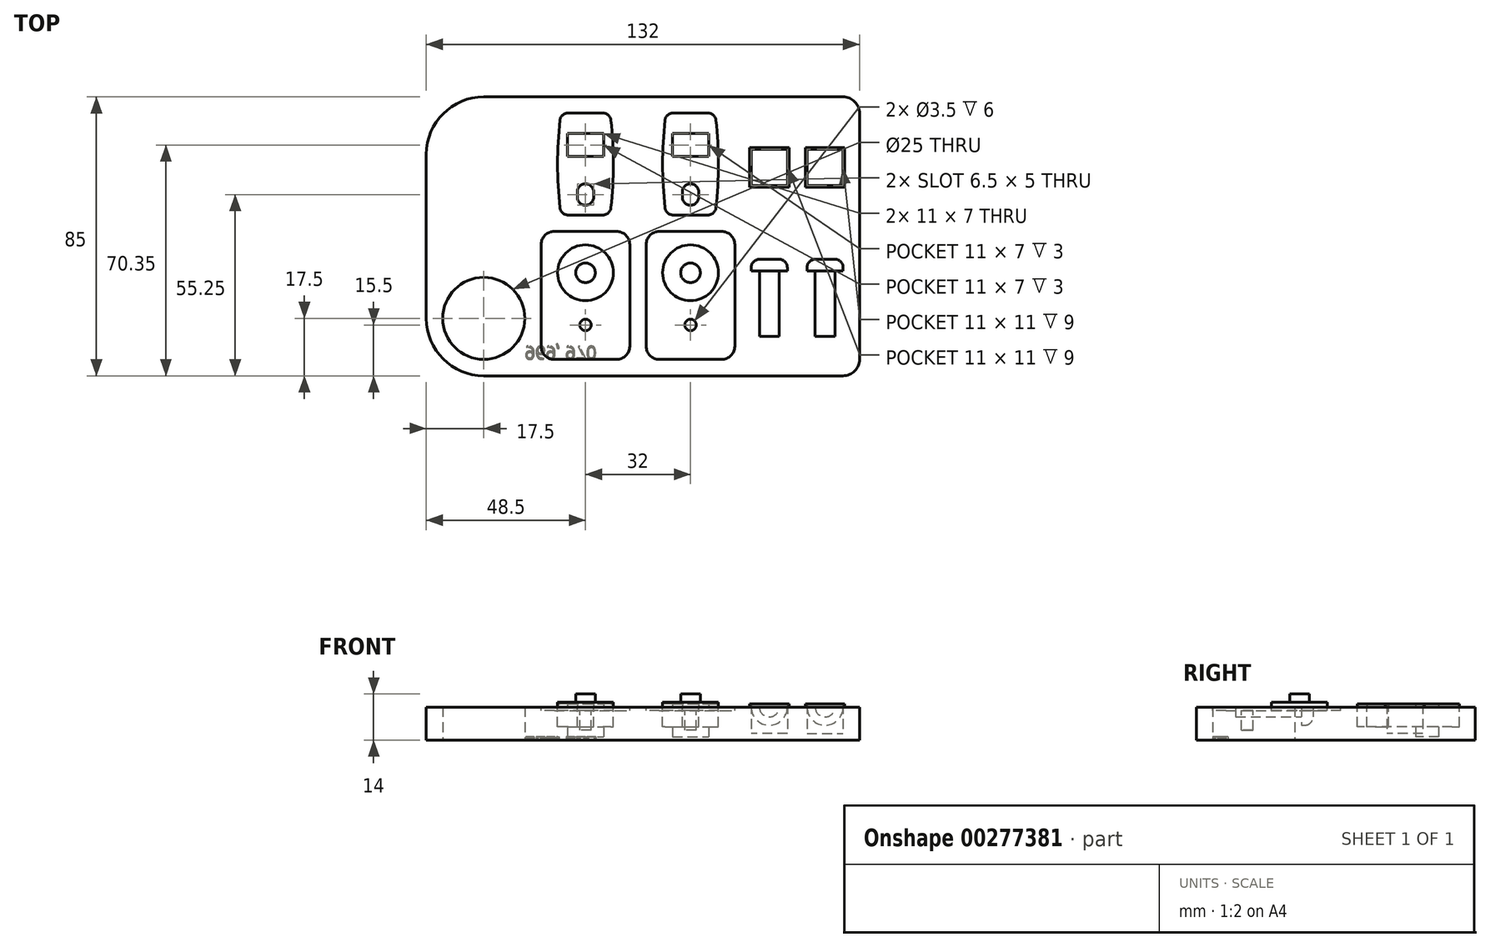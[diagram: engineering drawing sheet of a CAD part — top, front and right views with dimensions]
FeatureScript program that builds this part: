
annotation { "Feature Type Name" : "Feature", "Feature Type Description" : "" }
export const myFeature = defineFeature(function(context is Context, id is Id, definition is map)
    precondition{}
    {
        {
            var Q0;
            Q0=qCreatedBy(makeId("Top.planeOp"),FACE);
            var sketch = newSketch(context, id + "F0", { "sketchPlane" : qUnion([Q0])});
            skLineSegment(sketch, "E0.bottom", {"start": v(17.5, 0) * mm, "end": v(127, 0) * mm});
            skLineSegment(sketch, "E0.top", {"start": v(17.5, 85) * mm, "end": v(127, 85) * mm});
            skLineSegment(sketch, "E0.left", {"start": v(0, 17.5) * mm, "end": v(0, 67.5) * mm});
            skLineSegment(sketch, "E0.right", {"start": v(132, 5) * mm, "end": v(132, 80) * mm});
            skLineSegment(sketch, "E1.bottom", {"start": v(0, 0) * mm, "end": v(17.5, 0) * mm, "construction": true});
            skLineSegment(sketch, "E1.top", {"start": v(0, 17.5) * mm, "end": v(17.5, 17.5) * mm, "construction": true});
            skLineSegment(sketch, "E1.left", {"start": v(0, 0) * mm, "end": v(0, 17.5) * mm, "construction": true});
            skLineSegment(sketch, "E1.right", {"start": v(17.5, 0) * mm, "end": v(17.5, 17.5) * mm, "construction": true});
            skCircle(sketch, "E2", {"center": v(17.5, 17.5) * mm, "radius": 12.5 * mm});
            skPoint(sketch, "E3.visualSharp", {"position": v(0, 0) * mm});
            skArc(sketch, "E3.filletArc", {"start": v(0, 17.5) * mm, "mid": v(5.13, 5.13) * mm, "end": v(17.5, 0) * mm});
            skPoint(sketch, "E4.visualSharp", {"position": v(0, 85) * mm});
            skArc(sketch, "E4.filletArc", {"start": v(17.5, 85) * mm, "mid": v(5.13, 79.87) * mm, "end": v(0, 67.5) * mm});
            skPoint(sketch, "E5.visualSharp", {"position": v(132, 85) * mm});
            skArc(sketch, "E5.filletArc", {"start": v(132, 80) * mm, "mid": v(130.54, 83.54) * mm, "end": v(127, 85) * mm});
            skPoint(sketch, "E6.visualSharp", {"position": v(132, 0) * mm});
            skArc(sketch, "E6.filletArc", {"start": v(127, 0) * mm, "mid": v(130.54, 1.46) * mm, "end": v(132, 5) * mm});
            skSolve(sketch);
        }
        {
            var Q0;
            Q0=makeQuery(id+"F0.imprint","IMPRINT",FACE,{"disambiguationData":[TD([[makeQuery(id+"F0.imprint","IMPRINT",EDGE,{"derivedFrom":sQuery(id+"F0.wireOp",EDGE,"E0.bottom")}),1.0]])]});
            extrude(context, id + "F1", {"entities" : qUnion([Q0]), "depth" : 10 * mm});
        }
        {
            var Q0;
            Q0=makeQuery(id+"F1.opExtrude","CAP_FACE",FACE,{"disambiguationData":[OSD([sQuery(id+"F0.wireOp",EDGE,"E0.bottom"),sQuery(id+"F0.wireOp",EDGE,"E0.top"),sQuery(id+"F0.wireOp",EDGE,"E0.left"),sQuery(id+"F0.wireOp",EDGE,"E0.right"),sQuery(id+"F0.wireOp",EDGE,"E2"),sQuery(id+"F0.wireOp",EDGE,"E3.filletArc"),sQuery(id+"F0.wireOp",EDGE,"E4.filletArc"),sQuery(id+"F0.wireOp",EDGE,"E5.filletArc"),sQuery(id+"F0.wireOp",EDGE,"E6.filletArc")])],"isStart":false});
            var sketch = newSketch(context, id + "F2", { "sketchPlane" : qUnion([Q0])});
            skLineSegment(sketch, "E7.bottom", {"start": v(0, 0) * mm, "end": v(35, 0) * mm, "construction": true});
            skLineSegment(sketch, "E7.top", {"start": v(0, 5) * mm, "end": v(35, 5) * mm, "construction": true});
            skLineSegment(sketch, "E7.left", {"start": v(0, 0) * mm, "end": v(0, 5) * mm, "construction": true});
            skLineSegment(sketch, "E7.right", {"start": v(35, 0) * mm, "end": v(35, 5) * mm, "construction": true});
            skLineSegment(sketch, "E8.bottom", {"start": v(39, 5) * mm, "end": v(58, 5) * mm});
            skLineSegment(sketch, "E8.top", {"start": v(39, 44) * mm, "end": v(58, 44) * mm});
            skLineSegment(sketch, "E8.left", {"start": v(35, 9) * mm, "end": v(35, 40) * mm});
            skLineSegment(sketch, "E8.right", {"start": v(62, 9) * mm, "end": v(62, 40) * mm});
            skLineSegment(sketch, "E9", {"start": v(62, 5) * mm, "end": v(67, 5) * mm, "construction": true});
            skLineSegment(sketch, "E10.bottom", {"start": v(71, 5) * mm, "end": v(90, 5) * mm});
            skLineSegment(sketch, "E10.top", {"start": v(71, 44) * mm, "end": v(90, 44) * mm});
            skLineSegment(sketch, "E10.left", {"start": v(67, 9) * mm, "end": v(67, 40) * mm});
            skLineSegment(sketch, "E10.right", {"start": v(94, 9) * mm, "end": v(94, 40) * mm});
            skPoint(sketch, "E11.visualSharp", {"position": v(35, 44) * mm});
            skArc(sketch, "E11.filletArc", {"start": v(39, 44) * mm, "mid": v(36.17, 42.83) * mm, "end": v(35, 40) * mm});
            skPoint(sketch, "E12.visualSharp", {"position": v(62, 44) * mm});
            skArc(sketch, "E12.filletArc", {"start": v(62, 40) * mm, "mid": v(60.83, 42.83) * mm, "end": v(58, 44) * mm});
            skPoint(sketch, "E13.visualSharp", {"position": v(35, 5) * mm});
            skArc(sketch, "E13.filletArc", {"start": v(35, 9) * mm, "mid": v(36.17, 6.17) * mm, "end": v(39, 5) * mm});
            skPoint(sketch, "E14.visualSharp", {"position": v(62, 5) * mm});
            skArc(sketch, "E14.filletArc", {"start": v(58, 5) * mm, "mid": v(60.83, 6.17) * mm, "end": v(62, 9) * mm});
            skPoint(sketch, "E15.visualSharp", {"position": v(67, 5) * mm});
            skArc(sketch, "E15.filletArc", {"start": v(67, 9) * mm, "mid": v(68.17, 6.17) * mm, "end": v(71, 5) * mm});
            skPoint(sketch, "E16.visualSharp", {"position": v(67, 44) * mm});
            skArc(sketch, "E16.filletArc", {"start": v(71, 44) * mm, "mid": v(68.17, 42.83) * mm, "end": v(67, 40) * mm});
            skPoint(sketch, "E17.visualSharp", {"position": v(94, 44) * mm});
            skArc(sketch, "E17.filletArc", {"start": v(94, 40) * mm, "mid": v(92.83, 42.83) * mm, "end": v(90, 44) * mm});
            skPoint(sketch, "E18.visualSharp", {"position": v(94, 5) * mm});
            skArc(sketch, "E18.filletArc", {"start": v(90, 5) * mm, "mid": v(92.83, 6.17) * mm, "end": v(94, 9) * mm});
            skPoint(sketch, "E19.oppositeSnap0", {"position": v(48.5, 5) * mm});
            skLineSegment(sketch, "E19.bottom", {"start": v(35, 5) * mm, "end": v(48.5, 5) * mm, "construction": true});
            skLineSegment(sketch, "E19.top", {"start": v(35, 15.5) * mm, "end": v(48.5, 15.5) * mm, "construction": true});
            skLineSegment(sketch, "E19.left", {"start": v(35, 5) * mm, "end": v(35, 15.5) * mm, "construction": true});
            skLineSegment(sketch, "E19.right", {"start": v(48.5, 5) * mm, "end": v(48.5, 15.5) * mm, "construction": true});
            skLineSegment(sketch, "E20", {"start": v(48.5, 44) * mm, "end": v(48.5, 31.4) * mm, "construction": true});
            skLineSegment(sketch, "E21", {"start": v(80.5, 44) * mm, "end": v(80.5, 31.4) * mm, "construction": true});
            skLineSegment(sketch, "E22", {"start": v(80.5, 5) * mm, "end": v(80.5, 15.5) * mm, "construction": true});
            skCircle(sketch, "E23", {"center": v(48.5, 31.4) * mm, "radius": 8.5 * mm});
            skCircle(sketch, "E24", {"center": v(48.5, 31.4) * mm, "radius": 3 * mm});
            skCircle(sketch, "E25", {"center": v(48.5, 15.5) * mm, "radius": 1.75 * mm});
            skCircle(sketch, "E26", {"center": v(80.5, 15.5) * mm, "radius": 1.75 * mm});
            skCircle(sketch, "E27", {"center": v(80.5, 31.4) * mm, "radius": 3 * mm});
            skCircle(sketch, "E28", {"center": v(80.5, 31.4) * mm, "radius": 8.5 * mm});
            skLineSegment(sketch, "E29.bottom", {"start": v(94, 5) * mm, "end": v(104.5, 5) * mm, "construction": true});
            skLineSegment(sketch, "E29.top", {"start": v(94, 12) * mm, "end": v(104.5, 12) * mm, "construction": true});
            skLineSegment(sketch, "E29.left", {"start": v(94, 5) * mm, "end": v(94, 12) * mm, "construction": true});
            skLineSegment(sketch, "E29.right", {"start": v(104.5, 5) * mm, "end": v(104.5, 12) * mm, "construction": true});
            skLineSegment(sketch, "E30", {"start": v(104.5, 12) * mm, "end": v(121.5, 12) * mm, "construction": true});
            skLineSegment(sketch, "E31.bottom", {"start": v(104.5, 12) * mm, "end": v(107.5, 12) * mm});
            skLineSegment(sketch, "E31.left", {"start": v(104.5, 12) * mm, "end": v(104.5, 32) * mm});
            skLineSegment(sketch, "E31.right", {"start": v(107.5, 12) * mm, "end": v(107.5, 32) * mm});
            skLineSegment(sketch, "E32.bottom", {"start": v(107.5, 32) * mm, "end": v(110, 32) * mm});
            skLineSegment(sketch, "E32.top", {"start": v(104.5, 35.5) * mm, "end": v(107.5, 35.5) * mm});
            skLineSegment(sketch, "E32.left", {"start": v(104.5, 32) * mm, "end": v(104.5, 35.5) * mm});
            skLineSegment(sketch, "E32.right", {"start": v(110, 32) * mm, "end": v(110, 33) * mm});
            skPoint(sketch, "E33.visualSharp", {"position": v(110, 35.5) * mm});
            skArc(sketch, "E33.filletArc", {"start": v(110, 33) * mm, "mid": v(109.27, 34.77) * mm, "end": v(107.5, 35.5) * mm});
            skLineSegment(sketch, "E34.bottom", {"start": v(121.5, 12) * mm, "end": v(124.5, 12) * mm});
            skLineSegment(sketch, "E34.left", {"start": v(121.5, 12) * mm, "end": v(121.5, 32) * mm});
            skLineSegment(sketch, "E34.right", {"start": v(124.5, 12) * mm, "end": v(124.5, 32) * mm});
            skLineSegment(sketch, "E35.bottom", {"start": v(124.5, 32) * mm, "end": v(127, 32) * mm});
            skLineSegment(sketch, "E35.top", {"start": v(121.5, 35.5) * mm, "end": v(124.5, 35.5) * mm});
            skLineSegment(sketch, "E35.left", {"start": v(121.5, 32) * mm, "end": v(121.5, 35.5) * mm});
            skLineSegment(sketch, "E35.right", {"start": v(127, 32) * mm, "end": v(127, 33) * mm});
            skPoint(sketch, "E36.visualSharp", {"position": v(127, 35.5) * mm});
            skArc(sketch, "E36.filletArc", {"start": v(127, 33) * mm, "mid": v(126.27, 34.77) * mm, "end": v(124.5, 35.5) * mm});
            skLineSegment(sketch, "E37.bottom", {"start": v(35, 44) * mm, "end": v(41, 44) * mm, "construction": true});
            skLineSegment(sketch, "E37.top", {"start": v(35, 49) * mm, "end": v(41, 49) * mm, "construction": true});
            skLineSegment(sketch, "E37.left", {"start": v(35, 44) * mm, "end": v(35, 49) * mm, "construction": true});
            skLineSegment(sketch, "E37.right", {"start": v(41, 44) * mm, "end": v(41, 49) * mm, "construction": true});
            skLineSegment(sketch, "E38.bottom", {"start": v(43.22, 49) * mm, "end": v(53.78, 49) * mm});
            skLineSegment(sketch, "E38.top", {"start": v(43.22, 80.1) * mm, "end": v(53.78, 80.1) * mm});
            skLineSegment(sketch, "E38.left", {"start": v(41, 49) * mm, "end": v(41, 80.1) * mm, "construction": true});
            skLineSegment(sketch, "E38.right", {"start": v(56, 49) * mm, "end": v(56, 80.1) * mm, "construction": true});
            skLineSegment(sketch, "E39.bottom", {"start": v(67, 44) * mm, "end": v(73, 44) * mm, "construction": true});
            skLineSegment(sketch, "E39.top", {"start": v(67, 49) * mm, "end": v(73, 49) * mm, "construction": true});
            skLineSegment(sketch, "E39.left", {"start": v(67, 44) * mm, "end": v(67, 49) * mm, "construction": true});
            skLineSegment(sketch, "E39.right", {"start": v(73, 44) * mm, "end": v(73, 49) * mm, "construction": true});
            skLineSegment(sketch, "E40.bottom", {"start": v(75.22, 49) * mm, "end": v(85.78, 49) * mm});
            skLineSegment(sketch, "E40.top", {"start": v(75.22, 80.1) * mm, "end": v(85.78, 80.1) * mm});
            skLineSegment(sketch, "E40.left", {"start": v(73, 49) * mm, "end": v(73, 80.1) * mm, "construction": true});
            skLineSegment(sketch, "E40.right", {"start": v(88, 49) * mm, "end": v(88, 80.1) * mm, "construction": true});
            skLineSegment(sketch, "E41", {"start": v(41, 64.55) * mm, "end": v(40, 64.55) * mm});
            skLineSegment(sketch, "E42", {"start": v(56, 64.55) * mm, "end": v(57, 64.55) * mm});
            skLineSegment(sketch, "E43", {"start": v(73, 64.55) * mm, "end": v(72, 64.55) * mm});
            skLineSegment(sketch, "E44", {"start": v(88, 64.55) * mm, "end": v(89, 64.55) * mm});
            skArc(sketch, "E45", {"start": v(40.73, 77.87) * mm, "mid": v(40, 64.55) * mm, "end": v(40.73, 51.23) * mm});
            skArc(sketch, "E46", {"start": v(56.27, 51.23) * mm, "mid": v(57, 64.55) * mm, "end": v(56.27, 77.87) * mm});
            skArc(sketch, "E47", {"start": v(72.73, 77.87) * mm, "mid": v(72, 64.55) * mm, "end": v(72.73, 51.23) * mm});
            skArc(sketch, "E48", {"start": v(88.27, 51.23) * mm, "mid": v(89, 64.55) * mm, "end": v(88.27, 77.87) * mm});
            skPoint(sketch, "E49.visualSharp", {"position": v(56, 80.1) * mm});
            skArc(sketch, "E49.filletArc", {"start": v(56.27, 77.87) * mm, "mid": v(55.45, 79.46) * mm, "end": v(53.78, 80.1) * mm});
            skPoint(sketch, "E50.visualSharp", {"position": v(41, 80.1) * mm});
            skArc(sketch, "E50.filletArc", {"start": v(43.22, 80.1) * mm, "mid": v(41.55, 79.46) * mm, "end": v(40.73, 77.87) * mm});
            skPoint(sketch, "E51.visualSharp", {"position": v(41, 49) * mm});
            skArc(sketch, "E51.filletArc", {"start": v(40.73, 51.23) * mm, "mid": v(41.55, 49.64) * mm, "end": v(43.22, 49) * mm});
            skPoint(sketch, "E52.visualSharp", {"position": v(56, 49) * mm});
            skArc(sketch, "E52.filletArc", {"start": v(53.78, 49) * mm, "mid": v(55.45, 49.64) * mm, "end": v(56.27, 51.23) * mm});
            skPoint(sketch, "E53.visualSharp", {"position": v(73, 49) * mm});
            skArc(sketch, "E53.filletArc", {"start": v(72.73, 51.23) * mm, "mid": v(73.55, 49.64) * mm, "end": v(75.22, 49) * mm});
            skPoint(sketch, "E54.visualSharp", {"position": v(88, 49) * mm});
            skArc(sketch, "E54.filletArc", {"start": v(85.78, 49) * mm, "mid": v(87.45, 49.64) * mm, "end": v(88.27, 51.23) * mm});
            skPoint(sketch, "E55.visualSharp", {"position": v(88, 80.1) * mm});
            skArc(sketch, "E55.filletArc", {"start": v(88.27, 77.87) * mm, "mid": v(87.45, 79.46) * mm, "end": v(85.78, 80.1) * mm});
            skPoint(sketch, "E56.visualSharp", {"position": v(73, 80.1) * mm});
            skArc(sketch, "E56.filletArc", {"start": v(75.22, 80.1) * mm, "mid": v(73.55, 79.46) * mm, "end": v(72.73, 77.87) * mm});
            skLineSegment(sketch, "E57.bottom", {"start": v(41, 80.1) * mm, "end": v(43, 80.1) * mm, "construction": true});
            skLineSegment(sketch, "E57.top", {"start": v(41, 73.85) * mm, "end": v(43, 73.85) * mm, "construction": true});
            skLineSegment(sketch, "E57.left", {"start": v(41, 80.1) * mm, "end": v(41, 73.85) * mm, "construction": true});
            skLineSegment(sketch, "E57.right", {"start": v(43, 80.1) * mm, "end": v(43, 73.85) * mm, "construction": true});
            skLineSegment(sketch, "E58.bottom", {"start": v(73, 80.1) * mm, "end": v(75, 80.1) * mm, "construction": true});
            skLineSegment(sketch, "E58.top", {"start": v(73, 73.85) * mm, "end": v(75, 73.85) * mm, "construction": true});
            skLineSegment(sketch, "E58.left", {"start": v(73, 80.1) * mm, "end": v(73, 73.85) * mm, "construction": true});
            skLineSegment(sketch, "E58.right", {"start": v(75, 80.1) * mm, "end": v(75, 73.85) * mm, "construction": true});
            skLineSegment(sketch, "E59.bottom", {"start": v(43, 73.85) * mm, "end": v(54, 73.85) * mm});
            skLineSegment(sketch, "E59.top", {"start": v(43, 66.85) * mm, "end": v(54, 66.85) * mm});
            skLineSegment(sketch, "E59.left", {"start": v(43, 73.85) * mm, "end": v(43, 66.85) * mm});
            skLineSegment(sketch, "E59.right", {"start": v(54, 73.85) * mm, "end": v(54, 66.85) * mm});
            skLineSegment(sketch, "E60.bottom", {"start": v(75, 73.85) * mm, "end": v(86, 73.85) * mm});
            skLineSegment(sketch, "E60.top", {"start": v(75, 66.85) * mm, "end": v(86, 66.85) * mm});
            skLineSegment(sketch, "E60.left", {"start": v(75, 73.85) * mm, "end": v(75, 66.85) * mm});
            skLineSegment(sketch, "E60.right", {"start": v(86, 73.85) * mm, "end": v(86, 66.85) * mm});
            skLineSegment(sketch, "E61", {"start": v(48.5, 49) * mm, "end": v(48.5, 54.5) * mm, "construction": true});
            skLineSegment(sketch, "E62", {"start": v(80.5, 49) * mm, "end": v(80.5, 54.5) * mm, "construction": true});
            skLineSegment(sketch, "E63", {"start": v(48.5, 54.5) * mm, "end": v(48.5, 56) * mm, "construction": true});
            skLineSegment(sketch, "E64", {"start": v(80.5, 54.5) * mm, "end": v(80.5, 56) * mm, "construction": true});
            skArc(sketch, "E65.0.startCap", {"start": v(83, 54.5) * mm, "mid": v(80.5, 52) * mm, "end": v(78, 54.5) * mm});
            skArc(sketch, "E65.0.endCap", {"start": v(78, 56) * mm, "mid": v(80.5, 58.5) * mm, "end": v(83, 56) * mm});
            skLineSegment(sketch, "E65.0.left", {"start": v(78, 54.5) * mm, "end": v(78, 56) * mm});
            skLineSegment(sketch, "E65.0.right", {"start": v(83, 54.5) * mm, "end": v(83, 56) * mm});
            skArc(sketch, "E66.0.startCap", {"start": v(51, 54.5) * mm, "mid": v(48.5, 52) * mm, "end": v(46, 54.5) * mm});
            skArc(sketch, "E66.0.endCap", {"start": v(46, 56) * mm, "mid": v(48.5, 58.5) * mm, "end": v(51, 56) * mm});
            skLineSegment(sketch, "E66.0.left", {"start": v(46, 54.5) * mm, "end": v(46, 56) * mm});
            skLineSegment(sketch, "E66.0.right", {"start": v(51, 54.5) * mm, "end": v(51, 56) * mm});
            skLineSegment(sketch, "E67.bottom", {"start": v(104.5, 35.5) * mm, "end": v(98.5, 35.5) * mm, "construction": true});
            skLineSegment(sketch, "E67.top", {"start": v(104.5, 57.5) * mm, "end": v(98.5, 57.5) * mm, "construction": true});
            skLineSegment(sketch, "E67.left", {"start": v(104.5, 35.5) * mm, "end": v(104.5, 57.5) * mm, "construction": true});
            skLineSegment(sketch, "E67.right", {"start": v(98.5, 35.5) * mm, "end": v(98.5, 57.5) * mm, "construction": true});
            skLineSegment(sketch, "E68", {"start": v(98.5, 57.5) * mm, "end": v(115.5, 57.5) * mm, "construction": true});
            skLineSegment(sketch, "E69.bottom", {"start": v(98.5, 57.5) * mm, "end": v(110.5, 57.5) * mm});
            skLineSegment(sketch, "E69.top", {"start": v(98.5, 69.5) * mm, "end": v(110.5, 69.5) * mm});
            skLineSegment(sketch, "E69.left", {"start": v(98.5, 57.5) * mm, "end": v(98.5, 69.5) * mm});
            skLineSegment(sketch, "E69.right", {"start": v(110.5, 57.5) * mm, "end": v(110.5, 69.5) * mm});
            skLineSegment(sketch, "E70.bottom", {"start": v(115.5, 57.5) * mm, "end": v(127.5, 57.5) * mm});
            skLineSegment(sketch, "E70.top", {"start": v(115.5, 69.5) * mm, "end": v(127.5, 69.5) * mm});
            skLineSegment(sketch, "E70.left", {"start": v(115.5, 57.5) * mm, "end": v(115.5, 69.5) * mm});
            skLineSegment(sketch, "E70.right", {"start": v(127.5, 57.5) * mm, "end": v(127.5, 69.5) * mm});
            skLineSegment(sketch, "E71", {"start": v(98.5, 69.5) * mm, "end": v(110.5, 57.5) * mm, "construction": true});
            skLineSegment(sketch, "E72", {"start": v(115.5, 57.5) * mm, "end": v(127.5, 69.5) * mm, "construction": true});
            skLineSegment(sketch, "E73.bottom", {"start": v(110, 69) * mm, "end": v(99, 69) * mm});
            skLineSegment(sketch, "E73.top", {"start": v(110, 58) * mm, "end": v(99, 58) * mm});
            skLineSegment(sketch, "E73.left", {"start": v(110, 69) * mm, "end": v(110, 58) * mm});
            skLineSegment(sketch, "E73.right", {"start": v(99, 69) * mm, "end": v(99, 58) * mm});
            skPoint(sketch, "E73.middle", {"position": v(104.5, 63.5) * mm});
            skLineSegment(sketch, "E74.bottom", {"start": v(116, 69) * mm, "end": v(127, 69) * mm});
            skLineSegment(sketch, "E74.top", {"start": v(116, 58) * mm, "end": v(127, 58) * mm});
            skLineSegment(sketch, "E74.left", {"start": v(116, 69) * mm, "end": v(116, 58) * mm});
            skLineSegment(sketch, "E74.right", {"start": v(127, 69) * mm, "end": v(127, 58) * mm});
            skPoint(sketch, "E74.middle", {"position": v(121.5, 63.5) * mm});
            skSolve(sketch);
        }
        {
            var Q0;
            Q0=makeQuery(id+"F2.imprint","IMPRINT",FACE,{"disambiguationData":[TD([[makeQuery(id+"F2.imprint","IMPRINT",EDGE,{"derivedFrom":sQuery(id+"F2.wireOp",EDGE,"E8.bottom")}),1.0]])]});
            var Q1;
            Q1=makeQuery(id+"F2.imprint","IMPRINT",FACE,{"disambiguationData":[TD([[makeQuery(id+"F2.imprint","IMPRINT",EDGE,{"derivedFrom":sQuery(id+"F2.wireOp",EDGE,"E10.bottom")}),1.0]])]});
            extrude(context, id + "F3", {"entities" : qUnion([Q0, Q1]), "operationType" : NewBodyOperationType.REMOVE, "oppositeDirection" : true, "depth" : 1 * mm});
        }
        {
            var Q0;
            Q0=makeQuery(id+"F2.imprint","IMPRINT",FACE,{"disambiguationData":[TD([[makeQuery(id+"F2.imprint","IMPRINT",EDGE,{"derivedFrom":sQuery(id+"F2.wireOp",EDGE,"E25")}),1.0]])]});
            var Q1;
            Q1=makeQuery(id+"F2.imprint","IMPRINT",FACE,{"disambiguationData":[TD([[makeQuery(id+"F2.imprint","IMPRINT",EDGE,{"derivedFrom":sQuery(id+"F2.wireOp",EDGE,"E26")}),1.0]])]});
            var Q2;
            Q2=sQuery(id+"F2.wireOp",EDGE,"E25");
            var Q3;
            Q3=sQuery(id+"F2.wireOp",EDGE,"E26");
            extrude(context, id + "F4", {"entities" : qUnion([Q0, Q1]), "operationType" : NewBodyOperationType.REMOVE, "surfaceEntities" : qUnion([Q2, Q3]), "oppositeDirection" : true, "depth" : 7 * mm});
        }
        {
            var Q0;
            Q0=makeQuery(id+"F2.imprint","IMPRINT",FACE,{"disambiguationData":[TD([[makeQuery(id+"F2.imprint","IMPRINT",EDGE,{"derivedFrom":sQuery(id+"F2.wireOp",EDGE,"E27")}),-1.0]])]});
            var Q1;
            Q1=makeQuery(id+"F2.imprint","IMPRINT",FACE,{"disambiguationData":[TD([[makeQuery(id+"F2.imprint","IMPRINT",EDGE,{"derivedFrom":sQuery(id+"F2.wireOp",EDGE,"E23")}),1.0]])]});
            extrude(context, id + "F5", {"entities" : qUnion([Q0, Q1]), "operationType" : NewBodyOperationType.ADD, "depth" : 1.5 * mm});
        }
        {
            var Q0;
            Q0=makeQuery(id+"F2.imprint","IMPRINT",FACE,{"disambiguationData":[TD([[makeQuery(id+"F2.imprint","IMPRINT",EDGE,{"derivedFrom":sQuery(id+"F2.wireOp",EDGE,"E24")}),1.0]])]});
            var Q1;
            Q1=makeQuery(id+"F2.imprint","IMPRINT",FACE,{"disambiguationData":[TD([[makeQuery(id+"F2.imprint","IMPRINT",EDGE,{"derivedFrom":sQuery(id+"F2.wireOp",EDGE,"E27")}),1.0]])]});
            extrude(context, id + "F6", {"entities" : qUnion([Q0, Q1]), "operationType" : NewBodyOperationType.ADD, "depth" : 4 * mm});
        }
        {
            var Q0;
            Q0=makeQuery(id+"F2.imprint","IMPRINT",FACE,{"disambiguationData":[TD([[makeQuery(id+"F2.imprint","IMPRINT",EDGE,{"derivedFrom":sQuery(id+"F2.wireOp",EDGE,"E38.bottom")}),1.0]])]});
            var Q1;
            Q1=makeQuery(id+"F2.imprint","IMPRINT",FACE,{"disambiguationData":[TD([[makeQuery(id+"F2.imprint","IMPRINT",EDGE,{"derivedFrom":sQuery(id+"F2.wireOp",EDGE,"E40.bottom")}),1.0]])]});
            extrude(context, id + "F7", {"entities" : qUnion([Q0, Q1]), "operationType" : NewBodyOperationType.ADD, "depth" : 1 * mm});
        }
        {
            var Q0;
            Q0=makeQuery(id+"F2.imprint","IMPRINT",FACE,{"disambiguationData":[TD([[makeQuery(id+"F2.imprint","IMPRINT",EDGE,{"derivedFrom":sQuery(id+"F2.wireOp",EDGE,"E59.bottom")}),-1.0]])]});
            var Q1;
            Q1=makeQuery(id+"F2.imprint","IMPRINT",FACE,{"disambiguationData":[TD([[makeQuery(id+"F2.imprint","IMPRINT",EDGE,{"derivedFrom":sQuery(id+"F2.wireOp",EDGE,"E60.bottom")}),-1.0]])]});
            extrude(context, id + "F8", {"entities" : qUnion([Q0, Q1]), "operationType" : NewBodyOperationType.REMOVE, "oppositeDirection" : true, "depth" : 9 * mm});
        }
        {
            var Q0;
            Q0=makeQuery(id+"F2.imprint","IMPRINT",FACE,{"disambiguationData":[TD([[makeQuery(id+"F2.imprint","IMPRINT",EDGE,{"derivedFrom":sQuery(id+"F2.wireOp",EDGE,"E66.0.startCap")}),-1.0]])]});
            var Q1;
            Q1=makeQuery(id+"F2.imprint","IMPRINT",FACE,{"disambiguationData":[TD([[makeQuery(id+"F2.imprint","IMPRINT",EDGE,{"derivedFrom":sQuery(id+"F2.wireOp",EDGE,"E65.0.startCap")}),-1.0]])]});
            extrude(context, id + "F9", {"entities" : qUnion([Q0, Q1]), "operationType" : NewBodyOperationType.REMOVE, "oppositeDirection" : true, "depth" : 6 * mm});
        }
        {
            var Q0;
            Q0=makeQuery(id+"F2.imprint","IMPRINT",FACE,{"disambiguationData":[TD([[makeQuery(id+"F2.imprint","IMPRINT",EDGE,{"derivedFrom":sQuery(id+"F2.wireOp",EDGE,"E31.bottom")}),1.0]])]});
            var Q1;
            Q1=sQuery(id+"F2.wireOp",EDGE,"E31.left");
            revolve(context, id + "F10", {"operationType" : NewBodyOperationType.REMOVE, "entities" : qUnion([Q0]), "axis" : qUnion([Q1]), "revolveType" : RevolveType.FULL, "oppositeDirection" : true});
        }
        {
            var Q0;
            Q0=makeQuery(id+"F2.imprint","IMPRINT",FACE,{"disambiguationData":[TD([[makeQuery(id+"F2.imprint","IMPRINT",EDGE,{"derivedFrom":sQuery(id+"F2.wireOp",EDGE,"E34.bottom")}),1.0]])]});
            var Q1;
            Q1=sQuery(id+"F2.wireOp",EDGE,"E34.left");
            revolve(context, id + "F11", {"operationType" : NewBodyOperationType.REMOVE, "entities" : qUnion([Q0]), "axis" : qUnion([Q1]), "revolveType" : RevolveType.FULL, "oppositeDirection" : true});
        }
        {
            var Q0;
            Q0=makeQuery(id+"F2.imprint","IMPRINT",FACE,{"disambiguationData":[TD([[makeQuery(id+"F2.imprint","IMPRINT",EDGE,{"derivedFrom":sQuery(id+"F2.wireOp",EDGE,"E70.bottom")}),1.0]])]});
            var Q1;
            Q1=makeQuery(id+"F2.imprint","IMPRINT",FACE,{"disambiguationData":[TD([[makeQuery(id+"F2.imprint","IMPRINT",EDGE,{"derivedFrom":sQuery(id+"F2.wireOp",EDGE,"E69.bottom")}),1.0]])]});
            extrude(context, id + "F12", {"entities" : qUnion([Q0, Q1]), "operationType" : NewBodyOperationType.ADD, "depth" : 1 * mm});
        }
        {
            var Q0;
            Q0=makeQuery(id+"F2.imprint","IMPRINT",FACE,{"disambiguationData":[TD([[makeQuery(id+"F2.imprint","IMPRINT",EDGE,{"derivedFrom":sQuery(id+"F2.wireOp",EDGE,"E73.bottom")}),1.0]])]});
            var Q1;
            Q1=makeQuery(id+"F2.imprint","IMPRINT",FACE,{"disambiguationData":[TD([[makeQuery(id+"F2.imprint","IMPRINT",EDGE,{"derivedFrom":sQuery(id+"F2.wireOp",EDGE,"E74.bottom")}),-1.0]])]});
            extrude(context, id + "F13", {"entities" : qUnion([Q0, Q1]), "operationType" : NewBodyOperationType.REMOVE, "oppositeDirection" : true, "depth" : 8 * mm});
        }
        {
            var Q0;
            Q0=makeQuery(id+"F1.opExtrude","CAP_FACE",FACE,{"disambiguationData":[OSD([sQuery(id+"F0.wireOp",EDGE,"E0.bottom"),sQuery(id+"F0.wireOp",EDGE,"E0.top"),sQuery(id+"F0.wireOp",EDGE,"E0.left"),sQuery(id+"F0.wireOp",EDGE,"E0.right"),sQuery(id+"F0.wireOp",EDGE,"E2"),sQuery(id+"F0.wireOp",EDGE,"E3.filletArc"),sQuery(id+"F0.wireOp",EDGE,"E4.filletArc"),sQuery(id+"F0.wireOp",EDGE,"E5.filletArc"),sQuery(id+"F0.wireOp",EDGE,"E6.filletArc")])],"isStart":true});
            var sketch = newSketch(context, id + "F14", { "sketchPlane" : qUnion([Q0])});
            skLineSegment(sketch, "E75.bottom", {"start": v(0, 0) * mm, "end": v(30, 0) * mm, "construction": true});
            skLineSegment(sketch, "E75.top", {"start": v(0, -5) * mm, "end": v(30, -5) * mm, "construction": true});
            skLineSegment(sketch, "E75.left", {"start": v(0, 0) * mm, "end": v(0, -5) * mm, "construction": true});
            skLineSegment(sketch, "E75.right", {"start": v(30, 0) * mm, "end": v(30, -5) * mm, "construction": true});
            skText(sketch, "E76", { "text": "969, 970", "fontName": "OpenSans-Regular.ttf"});
            const initialGuessF14  = {"E76": [0.03, -0.009, 1, 0, 0.004]};
            skSetInitialGuess(sketch, initialGuessF14);
            skSolve(sketch);
        }
        {
            var Q0;
            Q0 = qSketchRegion(id + "F14", true);
            extrude(context, id + "F15", {"entities" : qUnion([Q0]), "operationType" : NewBodyOperationType.REMOVE, "oppositeDirection" : true, "depth" : 1 * mm});
        }
    });
